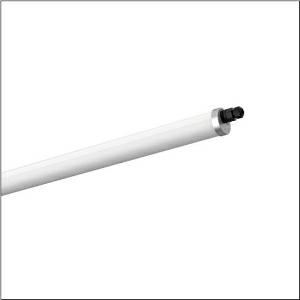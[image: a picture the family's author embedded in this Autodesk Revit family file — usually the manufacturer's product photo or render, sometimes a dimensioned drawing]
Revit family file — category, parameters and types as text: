
# Revit family: monsun_r__31_tube_51ft107n480a_b45d
name_source: partatom
category: Lighting Fixtures
units: mm (PartAtom-declared; Revit-internal decimal feet)

## family parameters
Cut with Voids When Loaded = No
Host = Face
Light Source = No
Part Type = Normal
Room Calculation Point = No
Round Connector Dimension = Use Diameter
Shared = No

## types (1)
- Monsun® 31 Tube (1 x LED, 8000 lm, 50 W, 4000K)
    Apparent Load = 50 VA
    CIE Flux Codes = 42 71 89 91 100
    Color Rendering = 80
    Color Temperature = 4000K
    Default Elevation = 1800 mm
    Description = Monsun® 31 Tube, tubular luminaire, primary optical cover: diffuser, of PMMA, light emission: direct distribution, primary light characteristic: symmetric, installation type: suspended mounting, surface-mounted, LED, rated luminous flux: 8.000lm, luminous efficacy: 160lm/W, light colour: 840, colour temperature: 4000K, control gear: ON/OFF, with with 1 terminal, 3-pole, max. 2.5mm², through-wiring: 3x 1.5mm², mains connection: 220..240V, AC, 50/60Hz, rated input power: 50W, housing, cylindrical, of PMMA, semi-transparent, matt white, with luminaire and ceiling fastening, V4A, mounting with brackets of stainless steel, length: 1.560mm, diameter: 75mm, end cap, of stainless steel (V4A), protection rating (complete): IP67/IP69K, insulation class (complete): insulation class I (protective earthing), certification: CE, UKCA, impact resistance: IK07, permissible operating ambient temperature: -20..+40°C, corresponds to IFS (International Featured Standards) requirements for safety and quality in the food industry, usage in unprotected outdoor areas possible with horizontal mounting, contact your sales advisor before using the luminaires in applications with unclear chemical exposure, large temperature fluctuations or condensation-forming humidity, packaging unit: 1 piece
    Height = 83 mm
    Lamp = 1 x LED
    Lamp Light Flux = 8000 lm
    Lamp Power = 50 W
    Lamp count = 1
    Length = 1560 mm
    Luminous efficacy = 160 lm/W
    Manufacturer = Siteco
    ModVariant = No
    Model = 51FT107N480A
    Mounting Place = Ceiling
    Mounting Type = Pendant
    Number of Poles = 1
    OnlyDefault = Yes
    Power Factor = 1
    Product Name = Monsun® 31 Tube
    Product group = tubular luminaire
    ProductGroupID = 907
    Protection Class = Protection class I
    RLX_Detail_Level = 1
    RLX_Emergency_Light_Flux = 0 lm
    RLX_Emergency_Type = 0
    RLX_Emergency_Type_DB = No
    RlxData = <blob elided: 25305 chars, md5=5c7792e1>
    Socket = socket
    Standby Power = 0 W
    System Light Flux = 8000 lm
    System Power = 50 W
    Type Comments = Product without accessories
    Type Image = l_1228461.jpg
    URL = http://relux.com
    VarID = ---
    Voltage = 0 V
    Weight = 0.00 kg
    Width = 75 mm

## geometry (parser evidence)
native form markers: Blend x4, Sweep x14
no freeform markers — native parametric forms only
